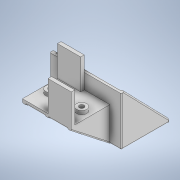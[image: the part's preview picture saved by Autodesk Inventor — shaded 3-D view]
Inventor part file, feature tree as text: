
AUTODESK INVENTOR PART (.ipt)
format: ipt  version: 2020 (Build 240168000, 168)  size: 391,680 bytes
history: native  units: in
note: dims shown in document units (in); Inventor stores cm internally (conversion verified against a paired STEP export)
features: extrude x15, sketch x15, fillet x3, mirror x1
ambient origin geometry x8: Origin, YZ Plane, XZ Plane, XY Plane, X Axis, Y Axis, Z Axis, Center Point
bodies: Solid1 (feature_tree)
feature tree (34):
  extrude  "Extrusion1"  Depth=1.2756in
  extrude  "Extrusion3"  Depth=0.1181in
  extrude  "Extrusion4"  Depth=0.1181in TaperAngle=0.0deg
  extrude  "Extrusion5"  Depth=0.1181in TaperAngle=0.0deg
  extrude  "Extrusion6"  Depth=0.1181in TaperAngle=0.0deg
  extrude  "Extrusion7"  Depth=0.3346in
  extrude  "Extrusion8"  Depth=0.1181in
  extrude  "Extrusion16"  Depth=0.2362in TaperAngle=0.0deg
  extrude  "Extrusion17"  Depth=0.2362in
  extrude  "Extrusion18"  Depth=0.1181in
  extrude  "Extrusion19"  Depth=0.1181in TaperAngle=0.0deg
  extrude  "Extrusion20"  Depth=0.1181in
  extrude  "Extrusion21"  Depth=0.1181in TaperAngle=0.0deg
  mirror  "Mirror1"
  extrude  "Extrusion22"  Depth=0.1575in
  extrude  "Extrusion23"  Depth=0.0394in TaperAngle=0.0deg
  fillet  "Fillet2"  Radius=0.5906in
  fillet  "Fillet3"  Radius=0.1181in
  fillet  "Fillet4"  Radius=0.6693in
  sketch  "Sketch1"  dims[d0=1.6142in d1=1.2756in]
  sketch  "Sketch3"  dims[d2=0.1181in d3=0.0in d8=0.1181in]
  sketch  "Sketch4"  dims[d9=0.1181in d10=1.0in d11=0.0in]
  sketch  "Sketch5"  dims[d12=0.8465in d13=0.1181in d14=0.0in]
  sketch  "Sketch6"  dims[d15=0.8465in d16=0.1181in d17=0.0in]
  sketch  "Sketch7"  dims[d20=0.3346in d21=0.3346in]
  sketch  "Sketch8"  dims[d22=0.1181in d23=0.0in d24=0.1575in]
  sketch  "Sketch17"  dims[d25=0.1575in d26=0.2362in d27=0.0in]
  sketch  "Sketch18"  dims[d28=0.2362in d29=0.2362in]
  sketch  "Sketch19"  dims[d30=0.1181in d31=0.0in d61=2.3622in]
  sketch  "Sketch20"  dims[d62=1.6181in d63=0.1181in d64=0.0in]
  sketch  "Sketch21"  dims[d65=0.1181in d66=0.1181in]
  sketch  "Sketch22"  dims[d67=0.1181in d68=1.4567in d69=0.0in]
  sketch  "Sketch23"  dims[d70=0.5906in d71=0.1575in]
  sketch  "Sketch24"  dims[d72=0.1575in d73=1.4567in d74=0.0in d75=0.5906in d76=0.1181in d77=0.6693in d78=0.0in d79=0.1575in d80=0.6693in d81=0.0in d82=0.3937in d83=0.2362in d84=0.1181in d85=0.0in d86=0.1181in d87=0.1181in d88=0.1181in d89=1.0in d90=0.0in d91=2.3622in d92=0.0in d93=0.0394in d94=0.0394in d95=0.0394in d58=0.0197in d59=0.0344in d60=0.0197in]
